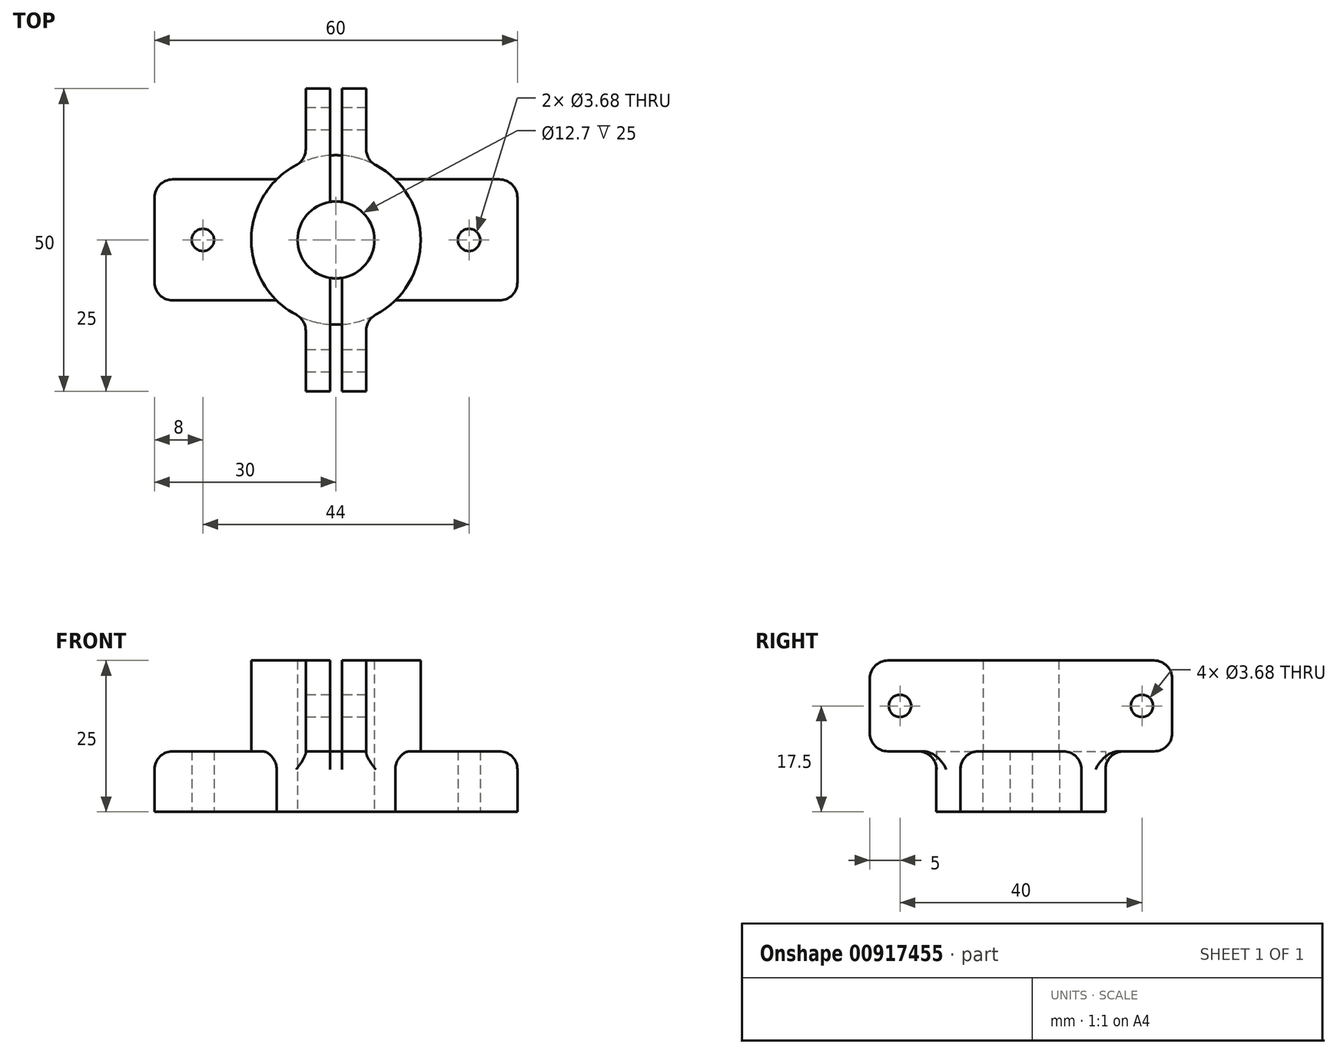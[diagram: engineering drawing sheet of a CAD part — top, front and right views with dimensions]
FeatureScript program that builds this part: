
annotation { "Feature Type Name" : "Feature", "Feature Type Description" : "" }
export const myFeature = defineFeature(function(context is Context, id is Id, definition is map)
    precondition{}
    {
        {
            var Q0;
            Q0=qCreatedBy(makeId("Top.planeOp"),FACE);
            var sketch = newSketch(context, id + "F0", { "sketchPlane" : qUnion([Q0])});
            skCircle(sketch, "E0", {"center": v(0, 0) * mm, "radius": 6.35 * mm});
            skCircle(sketch, "E1", {"center": v(0, 0) * mm, "radius": 14 * mm});
            skLineSegment(sketch, "E2.bottom", {"start": v(30, -10) * mm, "end": v(-30, -10) * mm});
            skLineSegment(sketch, "E2.top", {"start": v(30, 10) * mm, "end": v(-30, 10) * mm});
            skLineSegment(sketch, "E2.left", {"start": v(30, -10) * mm, "end": v(30, 10) * mm});
            skLineSegment(sketch, "E2.right", {"start": v(-30, -10) * mm, "end": v(-30, 10) * mm});
            skCircle(sketch, "E3", {"center": v(-22, 0) * mm, "radius": 1.84 * mm});
            skCircle(sketch, "E4", {"center": v(22, 0) * mm, "radius": 1.84 * mm});
            skSolve(sketch);
        }
        {
            var Q0;
            {var subQ0=sQuery(id+"F0.wireOp",EDGE,"E2.top");var subQ1=sQuery(id+"F0.wireOp",EDGE,"E1");var subQ2=makeQuery(id+"F0.imprint","INTERSECT",VERTEX,{"disambiguationData":[OD(0.0)],"derivedFrom":[subQ1,subQ0]});Q0=makeQuery(id+"F0.imprint","IMPRINT",FACE,{"disambiguationData":[TD([[makeQuery(id+"F0.imprint","IMPRINT",EDGE,{"disambiguationData":[TD([[subQ2,1.0]])],"derivedFrom":subQ1}),1.0]])]});}
            var Q1;
            Q1=makeQuery(id+"F0.imprint","IMPRINT",FACE,{"disambiguationData":[TD([[makeQuery(id+"F0.imprint","IMPRINT",EDGE,{"derivedFrom":sQuery(id+"F0.wireOp",EDGE,"E0")}),-1.0]])]});
            var Q2;
            {var subQ0=sQuery(id+"F0.wireOp",EDGE,"E2.bottom");var subQ1=sQuery(id+"F0.wireOp",EDGE,"E1");var subQ2=makeQuery(id+"F0.imprint","INTERSECT",VERTEX,{"disambiguationData":[OD(0.0)],"derivedFrom":[subQ1,subQ0]});Q2=makeQuery(id+"F0.imprint","IMPRINT",FACE,{"disambiguationData":[TD([[makeQuery(id+"F0.imprint","IMPRINT",EDGE,{"disambiguationData":[TD([[subQ2,-1.0]])],"derivedFrom":subQ1}),1.0]])]});}
            extrude(context, id + "F1", {"entities" : qUnion([Q0, Q1, Q2]), "depth" : 25 * mm, "offsetDistance" : 25 * mm});
        }
        {
            var Q0;
            {var subQ0=sQuery(id+"F0.wireOp",EDGE,"E2.right");Q0=makeQuery(id+"F0.imprint","IMPRINT",FACE,{"disambiguationData":[TD([[makeQuery(id+"F0.imprint","IMPRINT",EDGE,{"derivedFrom":subQ0}),-1.0]])]});}
            var Q1;
            {var subQ0=sQuery(id+"F0.wireOp",EDGE,"E2.left");Q1=makeQuery(id+"F0.imprint","IMPRINT",FACE,{"disambiguationData":[TD([[makeQuery(id+"F0.imprint","IMPRINT",EDGE,{"derivedFrom":subQ0}),1.0]])]});}
            extrude(context, id + "F2", {"entities" : qUnion([Q0, Q1]), "operationType" : NewBodyOperationType.ADD, "depth" : 10 * mm, "offsetDistance" : 25 * mm});
        }
        {
            var Q0;
            Q0=qCreatedBy(makeId("Right.planeOp"),FACE);
            var sketch = newSketch(context, id + "F3", { "sketchPlane" : qUnion([Q0])});
            skLineSegment(sketch, "E5.bottom", {"start": v(1.5, 25) * mm, "end": v(-1.5, 25) * mm});
            skLineSegment(sketch, "E5.top", {"start": v(1.5, 10) * mm, "end": v(-1.5, 10) * mm});
            skLineSegment(sketch, "E5.left", {"start": v(1.5, 25) * mm, "end": v(1.5, 10) * mm});
            skLineSegment(sketch, "E5.right", {"start": v(-1.5, 25) * mm, "end": v(-1.5, 10) * mm});
            skPoint(sketch, "E5.middle", {"position": v(0, 17.5) * mm});
            skLineSegment(sketch, "E6.bottom", {"start": v(25, 10) * mm, "end": v(-25, 10) * mm});
            skLineSegment(sketch, "E6.top", {"start": v(25, 25) * mm, "end": v(-25, 25) * mm});
            skLineSegment(sketch, "E6.left", {"start": v(25, 10) * mm, "end": v(25, 25) * mm});
            skLineSegment(sketch, "E6.right", {"start": v(-25, 10) * mm, "end": v(-25, 25) * mm});
            skCircle(sketch, "E7", {"center": v(-20, 17.5) * mm, "radius": 1.84 * mm});
            skPoint(sketch, "E7.centerSnap0", {"position": v(-25, 17.5) * mm});
            skCircle(sketch, "E8", {"center": v(20, 17.5) * mm, "radius": 1.84 * mm});
            skSolve(sketch);
        }
        {
            var Q0;
            {var subQ1=sQuery(id+"F3.wireOp",EDGE,"E5.right");Q0=makeQuery(id+"F3.imprint","IMPRINT",FACE,{"disambiguationData":[TD([[makeQuery(id+"F3.imprint","IMPRINT",EDGE,{"derivedFrom":subQ1}),-1.0]])]});}
            var Q1;
            {var subQ2=sQuery(id+"F3.wireOp",EDGE,"E5.left");Q1=makeQuery(id+"F3.imprint","IMPRINT",FACE,{"disambiguationData":[TD([[makeQuery(id+"F3.imprint","IMPRINT",EDGE,{"derivedFrom":subQ2}),1.0]])]});}
            var Q2;
            Q2=makeQuery(id+"F3.imprint","IMPRINT",FACE,{"disambiguationData":[TD([[makeQuery(id+"F3.imprint","IMPRINT",EDGE,{"derivedFrom":sQuery(id+"F3.wireOp",EDGE,"E5.bottom")}),1.0]])]});
            extrude(context, id + "F4", {"entities" : qUnion([Q0, Q1, Q2]), "operationType" : NewBodyOperationType.ADD, "depth" : 5 * mm, "offsetDistance" : 25 * mm, "hasSecondDirection" : true, "secondDirectionOppositeDirection" : true, "secondDirectionDepth" : 5 * mm});
        }
        {
            var Q0;
            Q0=makeQuery(id+"F4.opExtrude","SWEPT_FACE",FACE,{"disambiguationData":[OSD([sQuery(id+"F3.wireOp",EDGE,"E6.left")])]});
            var sketch = newSketch(context, id + "F5", { "sketchPlane" : qUnion([Q0])});
            skLineSegment(sketch, "E9.bottom", {"start": v(1, 25) * mm, "end": v(-1, 25) * mm});
            skLineSegment(sketch, "E9.top", {"start": v(1, 10) * mm, "end": v(-1, 10) * mm});
            skLineSegment(sketch, "E9.left", {"start": v(1, 25) * mm, "end": v(1, 10) * mm});
            skLineSegment(sketch, "E9.right", {"start": v(-1, 25) * mm, "end": v(-1, 10) * mm});
            skPoint(sketch, "E9.middle", {"position": v(0, 17.5) * mm});
            skPoint(sketch, "E9.middle.positionSnap0", {"position": v(0, 10) * mm});
            skPoint(sketch, "E9.middle.positionSnap1", {"position": v(-5, 17.5) * mm});
            skPoint(sketch, "E9.centerSnap0", {"position": v(0, 10) * mm});
            skPoint(sketch, "E9.centerSnap1", {"position": v(-5, 17.5) * mm});
            skSolve(sketch);
        }
        {
            var Q0;
            Q0=makeQuery(id+"F5.imprint","IMPRINT",FACE,{"disambiguationData":[TD([[makeQuery(id+"F5.imprint","IMPRINT",EDGE,{"derivedFrom":sQuery(id+"F5.wireOp",EDGE,"E9.bottom")}),-1.0]])]});
            extrude(context, id + "F6", {"entities" : qUnion([Q0]), "operationType" : NewBodyOperationType.REMOVE, "oppositeDirection" : true, "depth" : 50 * mm, "offsetDistance" : 25 * mm});
        }
        {
            var Q0;
            Q0=makeQuery(id+"F0.imprint","IMPRINT",FACE,{"disambiguationData":[TD([[makeQuery(id+"F0.imprint","IMPRINT",EDGE,{"derivedFrom":sQuery(id+"F0.wireOp",EDGE,"E0")}),1.0]])]});
            extrude(context, id + "F7", {"entities" : qUnion([Q0]), "operationType" : NewBodyOperationType.REMOVE, "depth" : 25 * mm, "offsetDistance" : 25 * mm});
        }
        {
            var Q0;
            {var subQ0=sQuery(id+"F0.wireOp",EDGE,"E2.top");Q0=makeQuery(id+"F2.opExtrude","CAP_EDGE",EDGE,{"disambiguationData":[OSD([subQ0]),TDD([makeQuery(id+"F0.imprint","IMPRINT",EDGE,{"disambiguationData":[TD([[makeQuery(id+"F0.imprint","INTERSECT",VERTEX,{"derivedFrom":[subQ0,sQuery(id+"F0.wireOp",EDGE,"E2.left")]}),-1.0]])],"derivedFrom":subQ0})])],"isStart":false});}
            var Q1;
            Q1=makeQuery(id+"F2.opExtrude","CAP_EDGE",EDGE,{"disambiguationData":[OSD([sQuery(id+"F0.wireOp",EDGE,"E2.left")])],"isStart":false});
            var Q2;
            {var subQ0=sQuery(id+"F0.wireOp",EDGE,"E2.bottom");Q2=makeQuery(id+"F2.opExtrude","CAP_EDGE",EDGE,{"disambiguationData":[OSD([subQ0]),TDD([makeQuery(id+"F0.imprint","IMPRINT",EDGE,{"disambiguationData":[TD([[makeQuery(id+"F0.imprint","INTERSECT",VERTEX,{"derivedFrom":[subQ0,sQuery(id+"F0.wireOp",EDGE,"E2.left")]}),-1.0]])],"derivedFrom":subQ0})])],"isStart":false});}
            var Q3;
            {var subQ0=sQuery(id+"F0.wireOp",EDGE,"E2.top");Q3=makeQuery(id+"F2.opExtrude","CAP_EDGE",EDGE,{"disambiguationData":[OSD([subQ0]),TDD([makeQuery(id+"F0.imprint","IMPRINT",EDGE,{"disambiguationData":[TD([[makeQuery(id+"F0.imprint","INTERSECT",VERTEX,{"derivedFrom":[subQ0,sQuery(id+"F0.wireOp",EDGE,"E2.right")]}),1.0]])],"derivedFrom":subQ0})])],"isStart":false});}
            var Q4;
            Q4=makeQuery(id+"F2.opExtrude","CAP_EDGE",EDGE,{"disambiguationData":[OSD([sQuery(id+"F0.wireOp",EDGE,"E2.right")])],"isStart":false});
            var Q5;
            {var subQ0=sQuery(id+"F0.wireOp",EDGE,"E2.bottom");Q5=makeQuery(id+"F2.opExtrude","CAP_EDGE",EDGE,{"disambiguationData":[OSD([subQ0]),TDD([makeQuery(id+"F0.imprint","IMPRINT",EDGE,{"disambiguationData":[TD([[makeQuery(id+"F0.imprint","INTERSECT",VERTEX,{"derivedFrom":[subQ0,sQuery(id+"F0.wireOp",EDGE,"E2.right")]}),1.0]])],"derivedFrom":subQ0})])],"isStart":false});}
            var Q6;
            {var subQ0=sQuery(id+"F0.wireOp",EDGE,"E2.top");var subQ1=sQuery(id+"F0.wireOp",EDGE,"E1");Q6=makeQuery(id+"F2.opExtrude","SWEPT_EDGE",EDGE,{"disambiguationData":[OSD([subQ1,subQ0]),TDD([makeQuery(id+"F0.imprint","INTERSECT",VERTEX,{"disambiguationData":[OD(0.0)],"derivedFrom":[subQ1,subQ0]})])]});}
            var Q7;
            {var subQ0=sQuery(id+"F0.wireOp",EDGE,"E1");Q7=makeQuery(id+"F2.opExtrude","CAP_EDGE",EDGE,{"disambiguationData":[OSD([subQ0]),TDD([makeQuery(id+"F0.imprint","IMPRINT",EDGE,{"disambiguationData":[TD([[makeQuery(id+"F0.imprint","INTERSECT",VERTEX,{"disambiguationData":[OD(1.0)],"derivedFrom":[subQ0,sQuery(id+"F0.wireOp",EDGE,"E2.top")]}),1.0]])],"derivedFrom":subQ0})])],"isStart":false});}
            var Q8;
            {var subQ0=sQuery(id+"F0.wireOp",EDGE,"E1");Q8=makeQuery(id+"F2.opExtrude","CAP_EDGE",EDGE,{"disambiguationData":[OSD([subQ0]),TDD([makeQuery(id+"F0.imprint","IMPRINT",EDGE,{"disambiguationData":[TD([[makeQuery(id+"F0.imprint","INTERSECT",VERTEX,{"disambiguationData":[OD(0.0)],"derivedFrom":[subQ0,sQuery(id+"F0.wireOp",EDGE,"E2.top")]}),-1.0]])],"derivedFrom":subQ0})])],"isStart":false});}
            var Q9;
            Q9=makeQuery(id+"F4.boolean.opBoolean","INTERSECT",EDGE,{"disambiguationData":[OD(1.0)],"derivedFrom":[makeQuery(id+"F1.opExtrude","SWEPT_FACE",FACE,{"disambiguationData":[OSD([sQuery(id+"F0.wireOp",EDGE,"E1")])]}),makeQuery(id+"F4.opExtrude","CAP_FACE",FACE,{"disambiguationData":[OSD([sQuery(id+"F3.wireOp",EDGE,"E5.bottom"),sQuery(id+"F3.wireOp",EDGE,"E5.top"),sQuery(id+"F3.wireOp",EDGE,"E6.bottom"),sQuery(id+"F3.wireOp",EDGE,"E6.top"),sQuery(id+"F3.wireOp",EDGE,"E6.left"),sQuery(id+"F3.wireOp",EDGE,"E6.right"),sQuery(id+"F3.wireOp",EDGE,"E7"),sQuery(id+"F3.wireOp",EDGE,"E8")])],"isStart":true})]});
            var Q10;
            Q10=makeQuery(id+"F4.boolean.opBoolean","INTERSECT",EDGE,{"disambiguationData":[OD(0.0)],"derivedFrom":[makeQuery(id+"F1.opExtrude","SWEPT_FACE",FACE,{"disambiguationData":[OSD([sQuery(id+"F0.wireOp",EDGE,"E1")])]}),makeQuery(id+"F4.opExtrude","CAP_FACE",FACE,{"disambiguationData":[OSD([sQuery(id+"F3.wireOp",EDGE,"E5.bottom"),sQuery(id+"F3.wireOp",EDGE,"E5.top"),sQuery(id+"F3.wireOp",EDGE,"E6.bottom"),sQuery(id+"F3.wireOp",EDGE,"E6.top"),sQuery(id+"F3.wireOp",EDGE,"E6.left"),sQuery(id+"F3.wireOp",EDGE,"E6.right"),sQuery(id+"F3.wireOp",EDGE,"E7"),sQuery(id+"F3.wireOp",EDGE,"E8")])],"isStart":true})]});
            var Q11;
            Q11=makeQuery(id+"F4.boolean.opBoolean","INTERSECT",EDGE,{"disambiguationData":[OD(0.0)],"derivedFrom":[makeQuery(id+"F1.opExtrude","SWEPT_FACE",FACE,{"disambiguationData":[OSD([sQuery(id+"F0.wireOp",EDGE,"E1")])]}),makeQuery(id+"F4.opExtrude","CAP_FACE",FACE,{"disambiguationData":[OSD([sQuery(id+"F3.wireOp",EDGE,"E5.bottom"),sQuery(id+"F3.wireOp",EDGE,"E5.top"),sQuery(id+"F3.wireOp",EDGE,"E6.bottom"),sQuery(id+"F3.wireOp",EDGE,"E6.top"),sQuery(id+"F3.wireOp",EDGE,"E6.left"),sQuery(id+"F3.wireOp",EDGE,"E6.right"),sQuery(id+"F3.wireOp",EDGE,"E7"),sQuery(id+"F3.wireOp",EDGE,"E8")])],"isStart":false})]});
            var Q12;
            Q12=makeQuery(id+"F4.boolean.opBoolean","INTERSECT",EDGE,{"disambiguationData":[OD(1.0)],"derivedFrom":[makeQuery(id+"F1.opExtrude","SWEPT_FACE",FACE,{"disambiguationData":[OSD([sQuery(id+"F0.wireOp",EDGE,"E1")])]}),makeQuery(id+"F4.opExtrude","CAP_FACE",FACE,{"disambiguationData":[OSD([sQuery(id+"F3.wireOp",EDGE,"E5.bottom"),sQuery(id+"F3.wireOp",EDGE,"E5.top"),sQuery(id+"F3.wireOp",EDGE,"E6.bottom"),sQuery(id+"F3.wireOp",EDGE,"E6.top"),sQuery(id+"F3.wireOp",EDGE,"E6.left"),sQuery(id+"F3.wireOp",EDGE,"E6.right"),sQuery(id+"F3.wireOp",EDGE,"E7"),sQuery(id+"F3.wireOp",EDGE,"E8")])],"isStart":false})]});
            var Q13;
            {var subQ0=sQuery(id+"F3.wireOp",EDGE,"E6.bottom");var subQ1=sQuery(id+"F3.wireOp",EDGE,"E5.top");var subQ2=makeQuery(id+"F4.opExtrude","SWEPT_FACE",FACE,{"disambiguationData":[OSD([subQ1,subQ0])]});var subQ3=makeQuery(id+"F1.opExtrude","SWEPT_FACE",FACE,{"disambiguationData":[OSD([sQuery(id+"F0.wireOp",EDGE,"E1")])]});Q13=makeQuery(id+"F6.boolean.opBoolean","SPLIT",EDGE,{"disambiguationData":[topologyDisambiguationEdgeConnected([subQ3,subQ2]),TD([makeQuery(id+"F6.opExtrude","SWEPT_FACE",FACE,{"disambiguationData":[OSD([sQuery(id+"F5.wireOp",EDGE,"E9.right")])]})])],"derivedFrom":makeQuery(id+"F4.boolean.opBoolean","INTERSECT",EDGE,{"disambiguationData":[OD(1.0)],"derivedFrom":[subQ3,subQ2]})});}
            var Q14;
            {var subQ0=sQuery(id+"F3.wireOp",EDGE,"E6.bottom");var subQ1=sQuery(id+"F3.wireOp",EDGE,"E5.top");var subQ2=makeQuery(id+"F4.opExtrude","SWEPT_FACE",FACE,{"disambiguationData":[OSD([subQ1,subQ0])]});var subQ3=makeQuery(id+"F1.opExtrude","SWEPT_FACE",FACE,{"disambiguationData":[OSD([sQuery(id+"F0.wireOp",EDGE,"E1")])]});Q14=makeQuery(id+"F6.boolean.opBoolean","SPLIT",EDGE,{"disambiguationData":[topologyDisambiguationEdgeConnected([subQ3,subQ2]),TD([makeQuery(id+"F6.opExtrude","SWEPT_FACE",FACE,{"disambiguationData":[OSD([sQuery(id+"F5.wireOp",EDGE,"E9.left")])]})])],"derivedFrom":makeQuery(id+"F4.boolean.opBoolean","INTERSECT",EDGE,{"disambiguationData":[OD(1.0)],"derivedFrom":[subQ3,subQ2]})});}
            var Q15;
            {var subQ0=sQuery(id+"F3.wireOp",EDGE,"E6.bottom");var subQ1=sQuery(id+"F3.wireOp",EDGE,"E5.top");var subQ2=makeQuery(id+"F4.opExtrude","SWEPT_FACE",FACE,{"disambiguationData":[OSD([subQ1,subQ0])]});var subQ3=makeQuery(id+"F1.opExtrude","SWEPT_FACE",FACE,{"disambiguationData":[OSD([sQuery(id+"F0.wireOp",EDGE,"E1")])]});Q15=makeQuery(id+"F6.boolean.opBoolean","SPLIT",EDGE,{"disambiguationData":[topologyDisambiguationEdgeConnected([subQ3,subQ2]),TD([makeQuery(id+"F6.opExtrude","SWEPT_FACE",FACE,{"disambiguationData":[OSD([sQuery(id+"F5.wireOp",EDGE,"E9.right")])]})])],"derivedFrom":makeQuery(id+"F4.boolean.opBoolean","INTERSECT",EDGE,{"disambiguationData":[OD(0.0)],"derivedFrom":[subQ3,subQ2]})});}
            var Q16;
            {var subQ0=sQuery(id+"F3.wireOp",EDGE,"E6.bottom");var subQ1=sQuery(id+"F3.wireOp",EDGE,"E5.top");var subQ2=makeQuery(id+"F4.opExtrude","SWEPT_FACE",FACE,{"disambiguationData":[OSD([subQ1,subQ0])]});var subQ3=makeQuery(id+"F1.opExtrude","SWEPT_FACE",FACE,{"disambiguationData":[OSD([sQuery(id+"F0.wireOp",EDGE,"E1")])]});Q16=makeQuery(id+"F6.boolean.opBoolean","SPLIT",EDGE,{"disambiguationData":[topologyDisambiguationEdgeConnected([subQ3,subQ2]),TD([makeQuery(id+"F6.opExtrude","SWEPT_FACE",FACE,{"disambiguationData":[OSD([sQuery(id+"F5.wireOp",EDGE,"E9.left")])]})])],"derivedFrom":makeQuery(id+"F4.boolean.opBoolean","INTERSECT",EDGE,{"disambiguationData":[OD(0.0)],"derivedFrom":[subQ3,subQ2]})});}
            var Q17;
            {var subQ0=sQuery(id+"F3.wireOp",EDGE,"E6.left");var subQ1=sQuery(id+"F3.wireOp",EDGE,"E6.bottom");Q17=makeQuery(id+"F6.boolean.opBoolean","SPLIT",EDGE,{"disambiguationData":[TD([makeQuery(id+"F6.opExtrude","SWEPT_FACE",FACE,{"disambiguationData":[OSD([sQuery(id+"F5.wireOp",EDGE,"E9.right")])]})])],"derivedFrom":makeQuery(id+"F4.opExtrude","SWEPT_EDGE",EDGE,{"disambiguationData":[OSD([subQ1,subQ0])]})});}
            var Q18;
            {var subQ0=sQuery(id+"F3.wireOp",EDGE,"E6.left");var subQ1=sQuery(id+"F3.wireOp",EDGE,"E6.bottom");Q18=makeQuery(id+"F6.boolean.opBoolean","SPLIT",EDGE,{"disambiguationData":[TD([makeQuery(id+"F6.opExtrude","SWEPT_FACE",FACE,{"disambiguationData":[OSD([sQuery(id+"F5.wireOp",EDGE,"E9.left")])]})])],"derivedFrom":makeQuery(id+"F4.opExtrude","SWEPT_EDGE",EDGE,{"disambiguationData":[OSD([subQ1,subQ0])]})});}
            var Q19;
            {var subQ0=sQuery(id+"F3.wireOp",EDGE,"E6.left");var subQ1=sQuery(id+"F3.wireOp",EDGE,"E6.top");Q19=makeQuery(id+"F6.boolean.opBoolean","SPLIT",EDGE,{"disambiguationData":[TD([makeQuery(id+"F6.opExtrude","SWEPT_FACE",FACE,{"disambiguationData":[OSD([sQuery(id+"F5.wireOp",EDGE,"E9.right")])]})])],"derivedFrom":makeQuery(id+"F4.opExtrude","SWEPT_EDGE",EDGE,{"disambiguationData":[OSD([subQ1,subQ0])]})});}
            var Q20;
            {var subQ0=sQuery(id+"F3.wireOp",EDGE,"E6.left");var subQ1=sQuery(id+"F3.wireOp",EDGE,"E6.top");Q20=makeQuery(id+"F6.boolean.opBoolean","SPLIT",EDGE,{"disambiguationData":[TD([makeQuery(id+"F6.opExtrude","SWEPT_FACE",FACE,{"disambiguationData":[OSD([sQuery(id+"F5.wireOp",EDGE,"E9.left")])]})])],"derivedFrom":makeQuery(id+"F4.opExtrude","SWEPT_EDGE",EDGE,{"disambiguationData":[OSD([subQ1,subQ0])]})});}
            var Q21;
            {var subQ0=sQuery(id+"F3.wireOp",EDGE,"E6.right");var subQ1=sQuery(id+"F3.wireOp",EDGE,"E6.top");Q21=makeQuery(id+"F6.boolean.opBoolean","SPLIT",EDGE,{"disambiguationData":[TD([makeQuery(id+"F6.opExtrude","SWEPT_FACE",FACE,{"disambiguationData":[OSD([sQuery(id+"F5.wireOp",EDGE,"E9.left")])]})])],"derivedFrom":makeQuery(id+"F4.opExtrude","SWEPT_EDGE",EDGE,{"disambiguationData":[OSD([subQ1,subQ0])]})});}
            var Q22;
            {var subQ0=sQuery(id+"F3.wireOp",EDGE,"E6.right");var subQ1=sQuery(id+"F3.wireOp",EDGE,"E6.top");Q22=makeQuery(id+"F6.boolean.opBoolean","SPLIT",EDGE,{"disambiguationData":[TD([makeQuery(id+"F6.opExtrude","SWEPT_FACE",FACE,{"disambiguationData":[OSD([sQuery(id+"F5.wireOp",EDGE,"E9.right")])]})])],"derivedFrom":makeQuery(id+"F4.opExtrude","SWEPT_EDGE",EDGE,{"disambiguationData":[OSD([subQ1,subQ0])]})});}
            var Q23;
            {var subQ0=sQuery(id+"F3.wireOp",EDGE,"E6.right");var subQ1=sQuery(id+"F3.wireOp",EDGE,"E6.bottom");Q23=makeQuery(id+"F6.boolean.opBoolean","SPLIT",EDGE,{"disambiguationData":[TD([makeQuery(id+"F6.opExtrude","SWEPT_FACE",FACE,{"disambiguationData":[OSD([sQuery(id+"F5.wireOp",EDGE,"E9.right")])]})])],"derivedFrom":makeQuery(id+"F4.opExtrude","SWEPT_EDGE",EDGE,{"disambiguationData":[OSD([subQ1,subQ0])]})});}
            var Q24;
            {var subQ0=sQuery(id+"F3.wireOp",EDGE,"E6.right");var subQ1=sQuery(id+"F3.wireOp",EDGE,"E6.bottom");Q24=makeQuery(id+"F6.boolean.opBoolean","SPLIT",EDGE,{"disambiguationData":[TD([makeQuery(id+"F6.opExtrude","SWEPT_FACE",FACE,{"disambiguationData":[OSD([sQuery(id+"F5.wireOp",EDGE,"E9.left")])]})])],"derivedFrom":makeQuery(id+"F4.opExtrude","SWEPT_EDGE",EDGE,{"disambiguationData":[OSD([subQ1,subQ0])]})});}
            var Q25;
            Q25=makeQuery(id+"F2.opExtrude","SWEPT_EDGE",EDGE,{"disambiguationData":[OSD([sQuery(id+"F0.wireOp",EDGE,"E2.top"),sQuery(id+"F0.wireOp",EDGE,"E2.right")])]});
            var Q26;
            Q26=makeQuery(id+"F2.opExtrude","SWEPT_EDGE",EDGE,{"disambiguationData":[OSD([sQuery(id+"F0.wireOp",EDGE,"E2.bottom"),sQuery(id+"F0.wireOp",EDGE,"E2.right")])]});
            var Q27;
            Q27=makeQuery(id+"F2.opExtrude","SWEPT_EDGE",EDGE,{"disambiguationData":[OSD([sQuery(id+"F0.wireOp",EDGE,"E2.top"),sQuery(id+"F0.wireOp",EDGE,"E2.left")])]});
            var Q28;
            Q28=makeQuery(id+"F2.opExtrude","SWEPT_EDGE",EDGE,{"disambiguationData":[OSD([sQuery(id+"F0.wireOp",EDGE,"E2.bottom"),sQuery(id+"F0.wireOp",EDGE,"E2.left")])]});
            var Q29;
            {var subQ0=sQuery(id+"F0.wireOp",EDGE,"E2.top");var subQ1=sQuery(id+"F0.wireOp",EDGE,"E1");Q29=makeQuery(id+"F2.opExtrude","SWEPT_EDGE",EDGE,{"disambiguationData":[OSD([subQ1,subQ0]),TDD([makeQuery(id+"F0.imprint","INTERSECT",VERTEX,{"disambiguationData":[OD(1.0)],"derivedFrom":[subQ1,subQ0]})])]});}
            fillet(context, id + "F8", {"entities" : qUnion([Q0, Q1, Q2, Q3, Q4, Q5, Q6, Q7, Q8, Q9, Q10, Q11, Q12, Q13, Q14, Q15, Q16, Q17, Q18, Q19, Q20, Q21, Q22, Q23, Q24, Q25, Q26, Q27, Q28, Q29]), "radius" : 3 * mm, "tangentPropagation" : true, "allowEdgeOverflow" : false});
        }
    });
